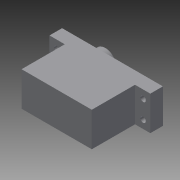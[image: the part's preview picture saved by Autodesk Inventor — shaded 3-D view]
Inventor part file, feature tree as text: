
AUTODESK INVENTOR PART (.ipt)
format: ipt  version: 2013 (Build 170138000, 138)  size: 107,008 bytes
history: native  units: mm
features: extrude x3, sketch x3
ambient origin geometry x8: Origin, YZ Plane, XZ Plane, XY Plane, X Axis, Y Axis, Z Axis, Center Point
bodies: Solid1 (feature_tree)
feature tree (6):
  extrude  "Extrusion1"  Depth=24.0mm
  extrude  "Extrusion2"  Depth=7.0mm
  extrude  "Extrusion3"  Depth=12.0mm
  sketch  "Sketch1"  dims[d0=39.0mm d1=24.0mm]
  sketch  "Sketch2"  dims[d2=56.0mm d3=7.0mm]
  sketch  "Sketch3"  dims[d4=19.0mm d5=0.0mm d6=12.0mm d7=18.0mm d8=3.0mm d9=6.0mm d10=0.0mm d11=3.0mm d12=3.0mm d13=3.0mm d14=3.0mm d15=4.0mm d16=4.0mm d17=4.5mm d18=4.5mm d19=10.0mm d20=0.0mm]
